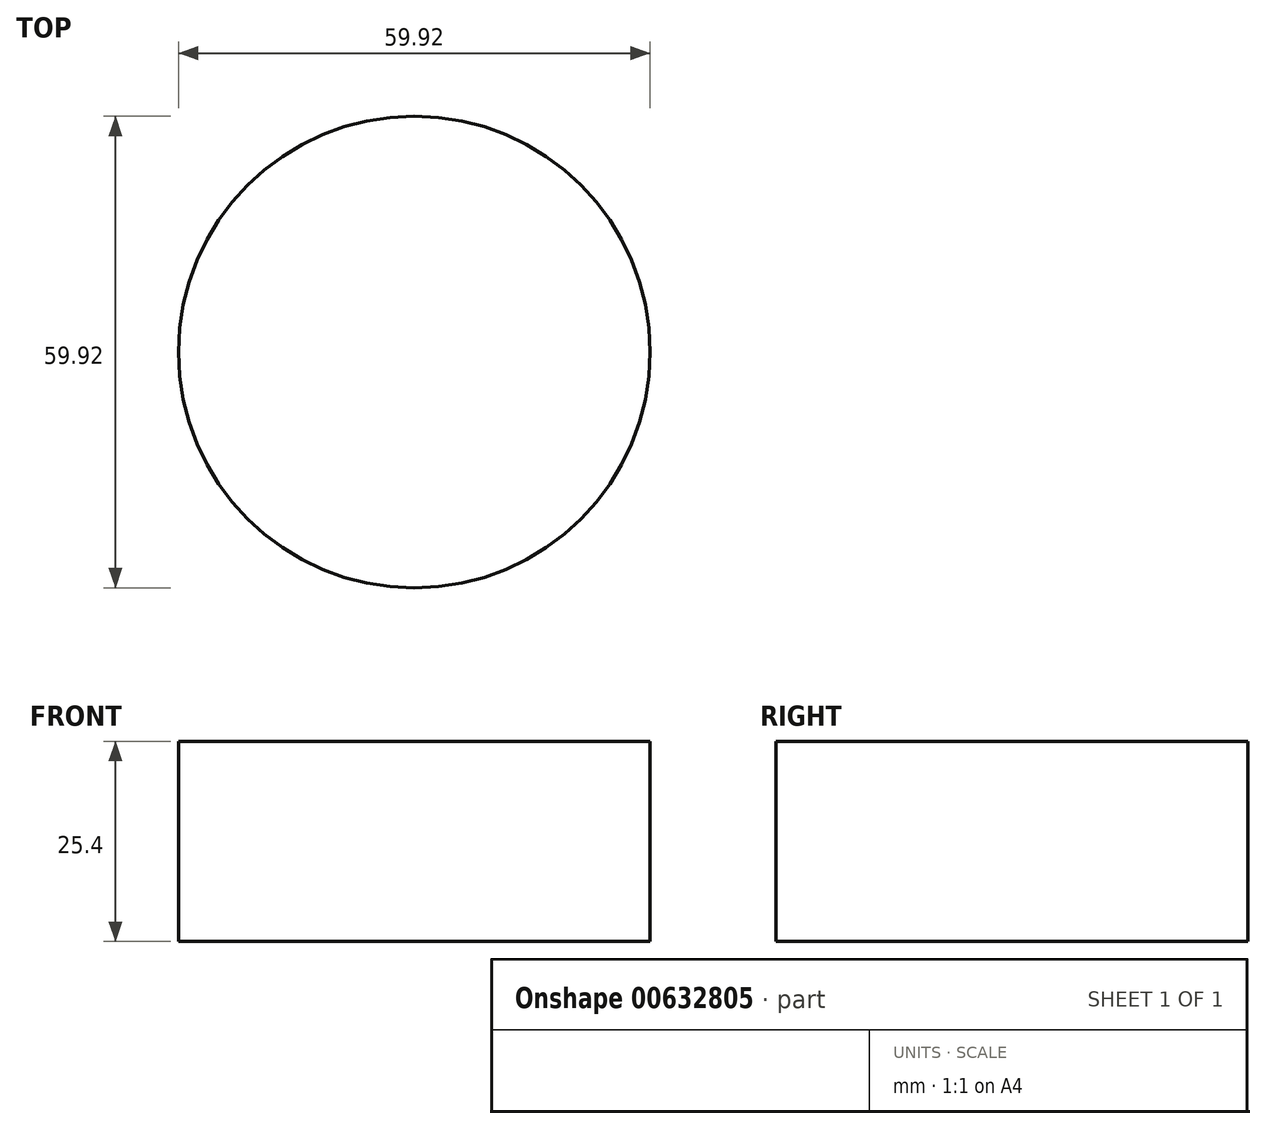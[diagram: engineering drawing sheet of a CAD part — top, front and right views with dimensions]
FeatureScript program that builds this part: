
annotation { "Feature Type Name" : "Feature", "Feature Type Description" : "" }
export const myFeature = defineFeature(function(context is Context, id is Id, definition is map)
    precondition{}
    {
        {
            var Q0;
            Q0=qCreatedBy(makeId("Top.planeOp"),FACE);
            var sketch = newSketch(context, id + "F0", { "sketchPlane" : qUnion([Q0])});
            skCircle(sketch, "E0", {"center": v(0, 0) * mm, "radius": 29.96 * mm});
            skSolve(sketch);
        }
        {
            var Q0;
            Q0=sQuery(id+"F0.wireOp",EDGE,"E0");
            extrude(context, id + "F1", {"bodyType" : ToolBodyType.SURFACE, "surfaceEntities" : qUnion([Q0]), "depth" : 25.4 * mm, "offsetDistance" : 25.4 * mm});
        }
    });
